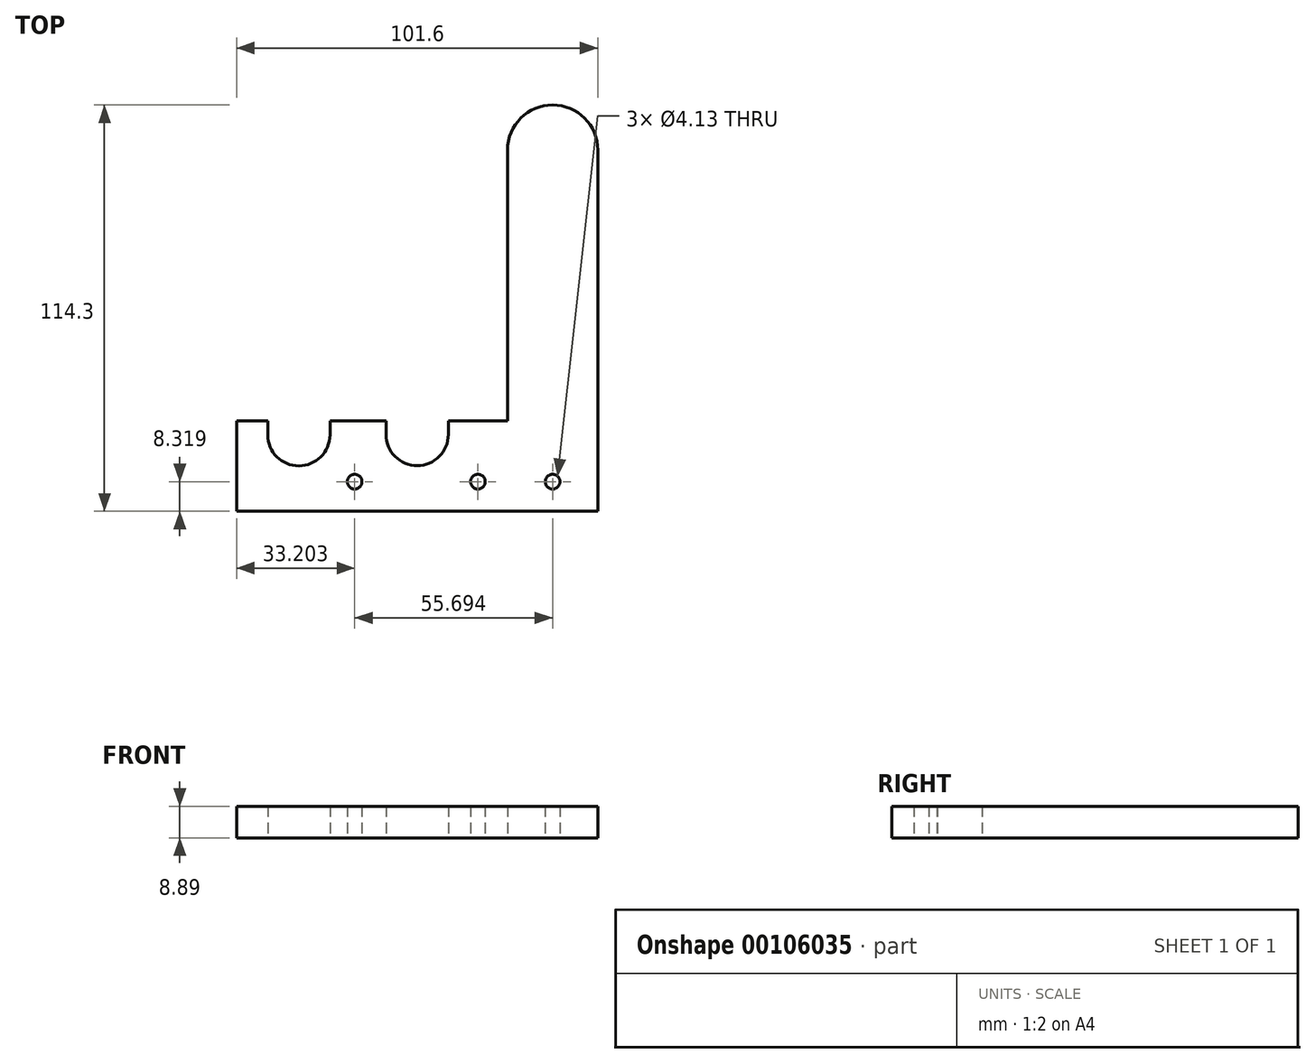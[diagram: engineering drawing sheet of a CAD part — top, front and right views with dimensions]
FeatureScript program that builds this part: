
annotation { "Feature Type Name" : "Feature", "Feature Type Description" : "" }
export const myFeature = defineFeature(function(context is Context, id is Id, definition is map)
    precondition{}
    {
        {
            var Q0;
            Q0=qCreatedBy(makeId("Top.planeOp"),FACE);
            var sketch = newSketch(context, id + "F0", { "sketchPlane" : qUnion([Q0])});
            skLineSegment(sketch, "E0", {"start": v(70.92, 0) * mm, "end": v(70.92, -25.4) * mm});
            skLineSegment(sketch, "E1.bottom", {"start": v(147.12, -25.4) * mm, "end": v(172.52, -25.4) * mm});
            skLineSegment(sketch, "E1.left", {"start": v(147.12, 0) * mm, "end": v(147.12, 76.2) * mm});
            skLineSegment(sketch, "E1.right", {"start": v(172.52, -25.4) * mm, "end": v(172.52, 76.2) * mm});
            skArc(sketch, "E2", {"start": v(172.52, 76.2) * mm, "mid": v(159.82, 88.9) * mm, "end": v(147.12, 76.2) * mm});
            skLineSegment(sketch, "E3", {"start": v(70.92, -25.4) * mm, "end": v(147.12, -25.4) * mm});
            skLineSegment(sketch, "E4", {"start": v(70.92, 0) * mm, "end": v(78.77, 0) * mm});
            skLineSegment(sketch, "E5", {"start": v(70.92, 0) * mm, "end": v(147.12, 0) * mm});
            skLineSegment(sketch, "E6", {"start": v(70.92, 0) * mm, "end": v(88.42, 0) * mm});
            skCircle(sketch, "E7", {"center": v(138.8, -17.08) * mm, "radius": 2.06 * mm});
            skCircle(sketch, "E8", {"center": v(104.12, -17.08) * mm, "radius": 2.06 * mm});
            skPoint(sketch, "E9.endSnap0", {"position": v(70.92, -12.7) * mm});
            skCircle(sketch, "E10", {"center": v(159.82, -17.08) * mm, "radius": 2.06 * mm});
            skCircle(sketch, "E11", {"center": v(88.42, -3.89) * mm, "radius": 8.76 * mm});
            skCircle(sketch, "E12", {"center": v(121.7, -3.8) * mm, "radius": 8.76 * mm});
            skLineSegment(sketch, "E13", {"start": v(79.66, -3.89) * mm, "end": v(79.66, 0) * mm});
            skPoint(sketch, "E13.endSnap0", {"position": v(79.67, 0) * mm});
            skLineSegment(sketch, "E14", {"start": v(112.94, -3.8) * mm, "end": v(112.94, 0) * mm});
            skLineSegment(sketch, "E15", {"start": v(130.47, -3.8) * mm, "end": v(130.47, 0) * mm});
            skLineSegment(sketch, "E16", {"start": v(97.19, -3.89) * mm, "end": v(97.19, 0) * mm});
            skSolve(sketch);
        }
        {
            var Q0;
            {var subQ8=sQuery(id+"F0.wireOp",EDGE,"E0");Q0=makeQuery(id+"F0.imprint","IMPRINT",FACE,{"disambiguationData":[TD([[makeQuery(id+"F0.imprint","IMPRINT",EDGE,{"derivedFrom":subQ8}),1.0]])]});}
            extrude(context, id + "F1", {"entities" : qUnion([Q0]), "depth" : 8.9 * mm});
        }
    });
